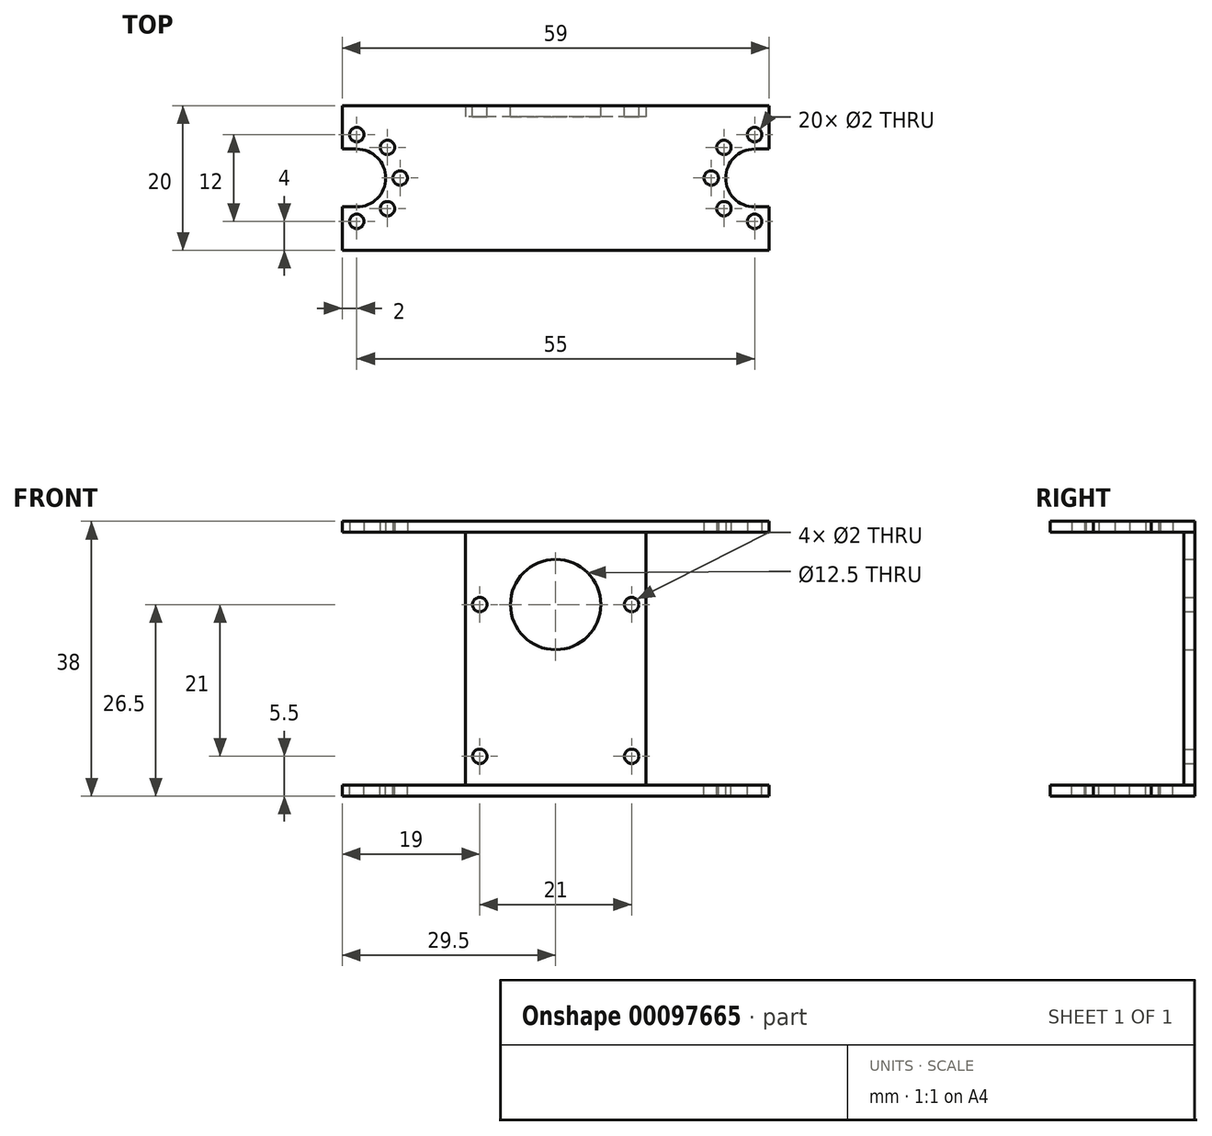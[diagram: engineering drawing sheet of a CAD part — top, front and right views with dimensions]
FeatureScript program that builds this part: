
annotation { "Feature Type Name" : "Feature", "Feature Type Description" : "" }
export const myFeature = defineFeature(function(context is Context, id is Id, definition is map)
    precondition{}
    {
        {
            var Q0;
            Q0=qCreatedBy(makeId("Top.planeOp"),FACE);
            var sketch = newSketch(context, id + "F0", { "sketchPlane" : qUnion([Q0])});
            skLineSegment(sketch, "E0.bottom", {"start": v(29.5, -10) * mm, "end": v(-29.5, -10) * mm});
            skLineSegment(sketch, "E0.top", {"start": v(29.5, 10) * mm, "end": v(-29.5, 10) * mm});
            skLineSegment(sketch, "E0.left", {"start": v(29.5, -10) * mm, "end": v(29.5, -4) * mm});
            skLineSegment(sketch, "E0.right", {"start": v(-29.5, -10) * mm, "end": v(-29.5, -4) * mm});
            skPoint(sketch, "E0.middle", {"position": v(0, 0) * mm});
            skCircle(sketch, "E1", {"center": v(-21.5, 0) * mm, "radius": 1 * mm});
            skLineSegment(sketch, "E2", {"start": v(-27.5, 4) * mm, "end": v(-29.5, 4) * mm});
            skLineSegment(sketch, "E3", {"start": v(-27.5, -4) * mm, "end": v(-29.5, -4) * mm});
            skArc(sketch, "E4.trimOffspring", {"start": v(-27.5, -4) * mm, "mid": v(-23.5, 0) * mm, "end": v(-27.5, 4) * mm});
            skLineSegment(sketch, "E5.trimOffspring", {"start": v(-29.5, 4) * mm, "end": v(-29.5, 10) * mm});
            skCircle(sketch, "E6.1.0", {"center": v(-23.26, 4.24) * mm, "radius": 1 * mm});
            skCircle(sketch, "E6.2.0", {"center": v(-27.5, 6) * mm, "radius": 1 * mm});
            skCircle(sketch, "E6.6.0", {"center": v(-27.5, -6) * mm, "radius": 1 * mm});
            skCircle(sketch, "E6.7.0", {"center": v(-23.26, -4.24) * mm, "radius": 1 * mm});
            skCircle(sketch, "E7.MirrorC", {"center": v(27.5, 6) * mm, "radius": 1 * mm});
            skCircle(sketch, "E8.MirrorC", {"center": v(23.26, 4.24) * mm, "radius": 1 * mm});
            skCircle(sketch, "E9.MirrorC", {"center": v(21.5, 0) * mm, "radius": 1 * mm});
            skCircle(sketch, "E10.MirrorC", {"center": v(23.26, -4.24) * mm, "radius": 1 * mm});
            skCircle(sketch, "E11.MirrorC", {"center": v(27.5, -6) * mm, "radius": 1 * mm});
            skLineSegment(sketch, "E12.MirrorCS", {"start": v(27.5, -4) * mm, "end": v(29.5, -4) * mm});
            skArc(sketch, "E13.MirrorCS", {"start": v(27.5, -4) * mm, "mid": v(23.5, 0) * mm, "end": v(27.5, 4) * mm});
            skLineSegment(sketch, "E14.MirrorCS", {"start": v(27.5, 4) * mm, "end": v(29.5, 4) * mm});
            skLineSegment(sketch, "E15.trimOffspring", {"start": v(29.5, 4) * mm, "end": v(29.5, 10) * mm});
            skSolve(sketch);
        }
        {
            var Q0;
            Q0 = qSketchRegion(id + "F0", true);
            extrude(context, id + "F1", {"entities" : qUnion([Q0]), "depth" : 1.5 * mm});
        }
        {
            var Q0;
            Q0=makeQuery(id+"F1.opExtrude","CAP_FACE",FACE,{"disambiguationData":[OSD([sQuery(id+"F0.wireOp",EDGE,"E0.bottom"),sQuery(id+"F0.wireOp",EDGE,"E0.top"),sQuery(id+"F0.wireOp",EDGE,"E0.left"),sQuery(id+"F0.wireOp",EDGE,"E1"),sQuery(id+"F0.wireOp",EDGE,"E2"),sQuery(id+"F0.wireOp",EDGE,"E3"),sQuery(id+"F0.wireOp",EDGE,"E6.1.0"),sQuery(id+"F0.wireOp",EDGE,"E6.2.0"),sQuery(id+"F0.wireOp",EDGE,"E6.6.0"),sQuery(id+"F0.wireOp",EDGE,"E6.7.0"),sQuery(id+"F0.wireOp",EDGE,"E7.MirrorC"),sQuery(id+"F0.wireOp",EDGE,"E8.MirrorC"),sQuery(id+"F0.wireOp",EDGE,"E9.MirrorC"),sQuery(id+"F0.wireOp",EDGE,"E10.MirrorC"),sQuery(id+"F0.wireOp",EDGE,"E11.MirrorC"),sQuery(id+"F0.wireOp",EDGE,"E12.MirrorCS"),sQuery(id+"F0.wireOp",EDGE,"E13.MirrorCS"),sQuery(id+"F0.wireOp",EDGE,"E14.MirrorCS"),sQuery(id+"F0.wireOp",EDGE,"E4.trimOffspring"),sQuery(id+"F0.wireOp",EDGE,"E0.right"),sQuery(id+"F0.wireOp",EDGE,"E15.trimOffspring"),sQuery(id+"F0.wireOp",EDGE,"E5.trimOffspring")])],"isStart":true});
            var sketch = newSketch(context, id + "F2", { "sketchPlane" : qUnion([Q0])});
            skLineSegment(sketch, "E16.bottom", {"start": v(12.5, -10) * mm, "end": v(-12.5, -10) * mm});
            skLineSegment(sketch, "E16.top", {"start": v(12.5, -8.5) * mm, "end": v(-12.5, -8.5) * mm});
            skLineSegment(sketch, "E16.left", {"start": v(12.5, -10) * mm, "end": v(12.5, -8.5) * mm});
            skLineSegment(sketch, "E16.right", {"start": v(-12.5, -10) * mm, "end": v(-12.5, -8.5) * mm});
            skPoint(sketch, "E16.middle", {"position": v(0, -9.25) * mm});
            skSolve(sketch);
        }
        {
            var Q0;
            Q0 = qSketchRegion(id + "F2", true);
            extrude(context, id + "F3", {"entities" : qUnion([Q0]), "operationType" : NewBodyOperationType.ADD, "depth" : (35 / 2) * mm});
        }
        {
            var Q0;
            Q0=qCreatedBy(makeId("Top.planeOp"),FACE);
            cPlane(context, id + "F4", {"entities" : qUnion([Q0]), "cplaneType" : CPlaneType.OFFSET, "offset" : (35 / 2) * mm, "oppositeDirection" : true, "width" : 150 * mm, "height" : 150 * mm});
        }
        {
            var Q0;
            Q0=makeQuery(id+"F1.opExtrude","SWEPT_BODY",BODY,{"disambiguationData":[OSD([sQuery(id+"F0.wireOp",EDGE,"E0.bottom"),sQuery(id+"F0.wireOp",EDGE,"E0.top"),sQuery(id+"F0.wireOp",EDGE,"E0.left"),sQuery(id+"F0.wireOp",EDGE,"E1"),sQuery(id+"F0.wireOp",EDGE,"E2"),sQuery(id+"F0.wireOp",EDGE,"E3"),sQuery(id+"F0.wireOp",EDGE,"E6.1.0"),sQuery(id+"F0.wireOp",EDGE,"E6.2.0"),sQuery(id+"F0.wireOp",EDGE,"E6.6.0"),sQuery(id+"F0.wireOp",EDGE,"E6.7.0"),sQuery(id+"F0.wireOp",EDGE,"E7.MirrorC"),sQuery(id+"F0.wireOp",EDGE,"E8.MirrorC"),sQuery(id+"F0.wireOp",EDGE,"E9.MirrorC"),sQuery(id+"F0.wireOp",EDGE,"E10.MirrorC"),sQuery(id+"F0.wireOp",EDGE,"E11.MirrorC"),sQuery(id+"F0.wireOp",EDGE,"E12.MirrorCS"),sQuery(id+"F0.wireOp",EDGE,"E13.MirrorCS"),sQuery(id+"F0.wireOp",EDGE,"E14.MirrorCS"),sQuery(id+"F0.wireOp",EDGE,"E4.trimOffspring"),sQuery(id+"F0.wireOp",EDGE,"E0.right"),sQuery(id+"F0.wireOp",EDGE,"E15.trimOffspring"),sQuery(id+"F0.wireOp",EDGE,"E5.trimOffspring")])]});
            var Q1;
            Q1=qCreatedBy(id+"F4.planeOp",FACE);
            mirror(context, id + "F5", {"operationType" : NewBodyOperationType.ADD, "entities" : qUnion([Q0]), "mirrorPlane" : qUnion([Q1])});
        }
        {
            var Q0;
            {var subQ0=makeQuery(id+"F3.boolean.opBoolean","MERGE",FACE,{"derivedFrom":[makeQuery(id+"F1.opExtrude","SWEPT_FACE",FACE,{"disambiguationData":[OSD([sQuery(id+"F0.wireOp",EDGE,"E0.top")])]}),makeQuery(id+"F3.opExtrude","SWEPT_FACE",FACE,{"disambiguationData":[OSD([sQuery(id+"F2.wireOp",EDGE,"E16.bottom")])]})]});Q0=makeQuery(id+"F5.boolean.opBoolean","MERGE",FACE,{"derivedFrom":[subQ0,makeQuery(id+"F5.opPattern","COPY",FACE,{"derivedFrom":subQ0,"instanceName":"1"})]});}
            var sketch = newSketch(context, id + "F6", { "sketchPlane" : qUnion([Q0])});
            skLineSegment(sketch, "E17", {"start": v(-12.5, -17.5) * mm, "end": v(12.5, -17.5) * mm, "construction": true});
            skLineSegment(sketch, "E18", {"start": v(0, 1.5) * mm, "end": v(0, -36.5) * mm, "construction": true});
            skCircle(sketch, "E19", {"center": v(10.5, -10) * mm, "radius": 1 * mm});
            skCircle(sketch, "E20", {"center": v(10.5, -31) * mm, "radius": 1 * mm});
            skCircle(sketch, "E21", {"center": v(0, -10) * mm, "radius": 6.25 * mm});
            skCircle(sketch, "E22.MirrorC", {"center": v(-10.5, -10) * mm, "radius": 1 * mm});
            skCircle(sketch, "E23.MirrorC", {"center": v(-10.5, -31) * mm, "radius": 1 * mm});
            skSolve(sketch);
        }
        {
            var Q0;
            Q0 = qSketchRegion(id + "F6", true);
            extrude(context, id + "F7", {"entities" : qUnion([Q0]), "operationType" : NewBodyOperationType.REMOVE, "endBound" : BoundingType.UP_TO_NEXT, "oppositeDirection" : true, "depth" : 25 * mm});
        }
    });
